# Revit family: Mélange Gaz 500L VERTICAL
name_source: partatom
category: Equipement de génie climatique
units: mm (PartAtom-declared; Revit-internal decimal feet)

## family parameters
Basée sur le plan de construction = Non
Classification = Aucun
Cote de connecteur circulaire = Utiliser le diamètre
Couper avec des vides une fois chargée = Non
Partagée = Non
Repere pour localisation dans la piece = Non
Toujours verticalement = Oui
Type d'élément = Normal

## types (2) — shared parameters
Rayon Cuve = 325 mm  [stored 1.06627 ft]
Ø Diamètre Cuve = 650 mm  [stored 2.13255 ft]
zero-valued in all types: Elévation par défaut

## per-type parameters (varying)
| type | Fabricant | Hauteur de pied | Ht Fond bombé | Ht ballon sans pied | Modèle |
| 500L | Mil's | 356 mm  [stored 1.16798 ft] | 212 mm  [stored 0.695538 ft] | 1634 mm  [stored 5.36089 ft] | Mélange Gaz 500L VERTICAL |
| 200L |  | 317 mm  [stored 1.04003 ft] | 173 mm  [stored 0.567585 ft] | 1310 mm  [stored 4.2979 ft] |  |

note: [stored X ft] marks values corroborated as IEEE doubles in the binary element streams (Revit-internal decimal feet)
